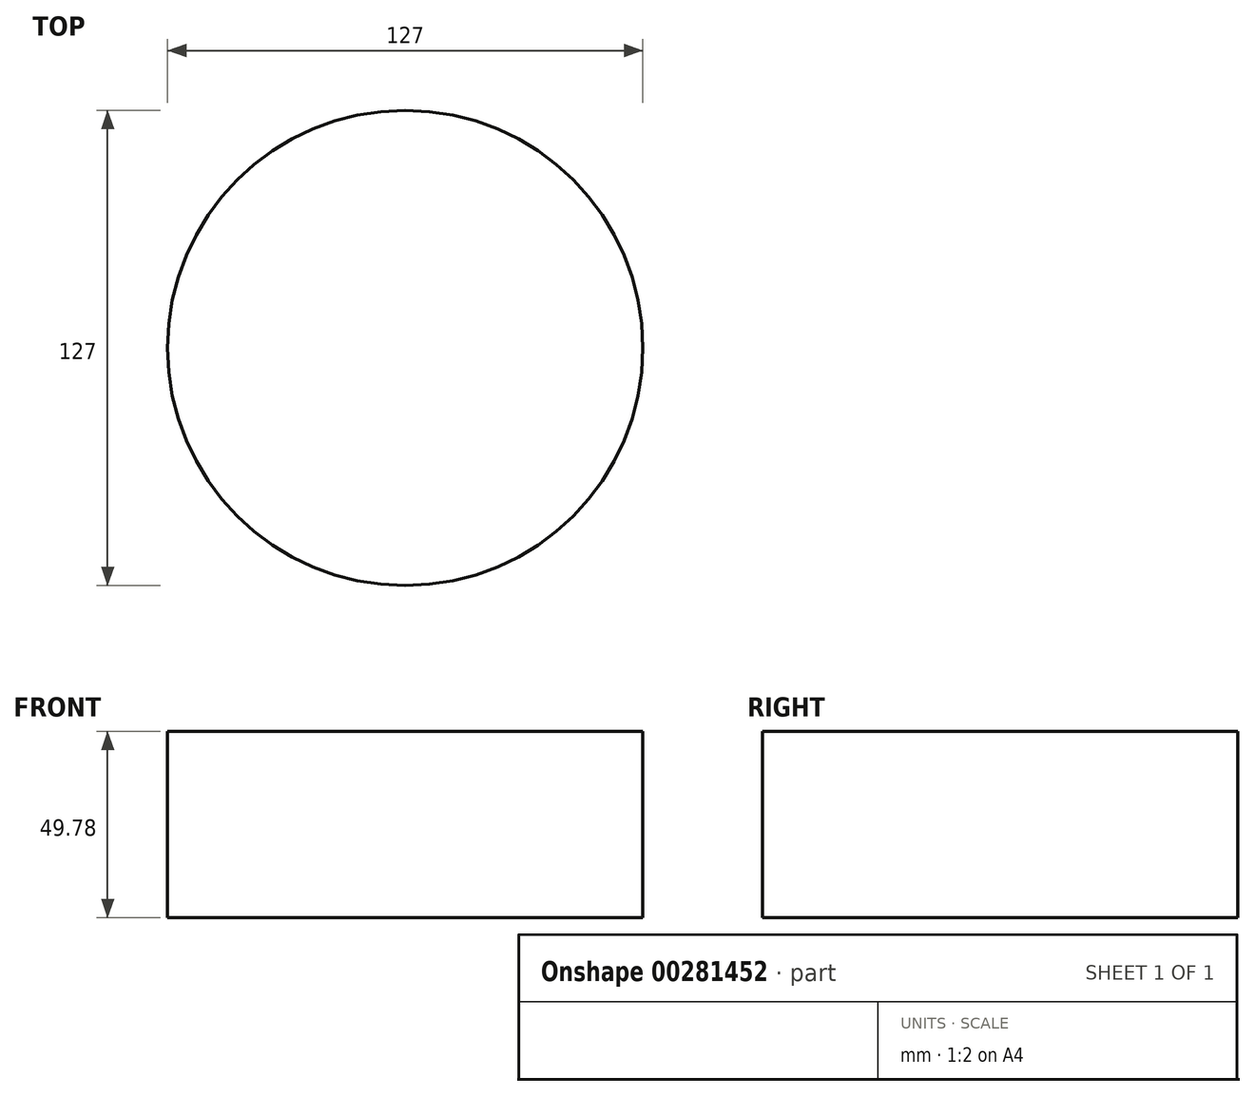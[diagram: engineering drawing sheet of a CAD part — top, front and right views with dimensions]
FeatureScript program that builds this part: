
annotation { "Feature Type Name" : "Feature", "Feature Type Description" : "" }
export const myFeature = defineFeature(function(context is Context, id is Id, definition is map)
    precondition{}
    {
        {
            var Q0;
            Q0=qCreatedBy(makeId("Top.planeOp"),FACE);
            var sketch = newSketch(context, id + "F0", { "sketchPlane" : qUnion([Q0])});
            skCircle(sketch, "E0", {"center": v(0, 0) * mm, "radius": 63.5 * mm});
            skSolve(sketch);
        }
        {
            var Q0;
            Q0=qCreatedBy(makeId("Top.planeOp"),FACE);
            cPlane(context, id + "F1", {"entities" : qUnion([Q0]), "cplaneType" : CPlaneType.OFFSET, "offset" : 49.78 * mm, "width" : 152.4 * mm, "height" : 152.4 * mm});
        }
        {
            var Q0;
            Q0=qCreatedBy(id+"F1.planeOp",FACE);
            var sketch = newSketch(context, id + "F2", { "sketchPlane" : qUnion([Q0])});
            skCircle(sketch, "E1.0", {"center": v(0, 0) * mm, "radius": 63.5 * mm});
            skSolve(sketch);
        }
        {
            var Q0;
            Q0=qCreatedBy(makeId("Front.planeOp"),FACE);
            var sketch = newSketch(context, id + "F3", { "sketchPlane" : qUnion([Q0])});
            skPoint(sketch, "E2.orphan", {"position": v(63.5, 0) * mm});
            skPoint(sketch, "E3.orphan", {"position": v(-63.5, 49.78) * mm});
            skPoint(sketch, "E4.0.end.orphan", {"position": v(63.5, 49.78) * mm});
            skPoint(sketch, "E5.0.start.orphan", {"position": v(-63.5, 0) * mm});
            skArc(sketch, "E6", {"start": v(63.5, 49.78) * mm, "mid": v(24.76, 33.8) * mm, "end": v(0, 0) * mm});
            skSolve(sketch);
        }
        {
            var Q0;
            Q0=makeQuery(id+"F0.imprint","IMPRINT",FACE,{"disambiguationData":[TD([[makeQuery(id+"F0.imprint","IMPRINT",EDGE,{"derivedFrom":sQuery(id+"F0.wireOp",EDGE,"E0")}),1.0]])]});
            var Q1;
            Q1=makeQuery(id+"F2.imprint","IMPRINT",FACE,{"disambiguationData":[TD([[makeQuery(id+"F2.imprint","IMPRINT",EDGE,{"derivedFrom":sQuery(id+"F2.wireOp",EDGE,"E1.0")}),1.0]])]});
            var Q2;
            Q2=sQuery(id+"F3.wireOp",EDGE,"XZxfceJF-F9cA-zvLT-lmJa-7WOxV4JV3vpH");
            loft(context, id + "F4", {"addGuides" : true, "sheetProfilesArray" : [{ "sheetProfileEntities" : qUnion([Q0]) }, { "sheetProfileEntities" : qUnion([Q1]) }], "guidesArray" : [{ "guideEntities" : qUnion([Q2]), "guideDerivativeType" : LoftGuideDerivativeType.DEFAULT, "guideDerivativeMagnitude" : 1 }]});
        }
    });
